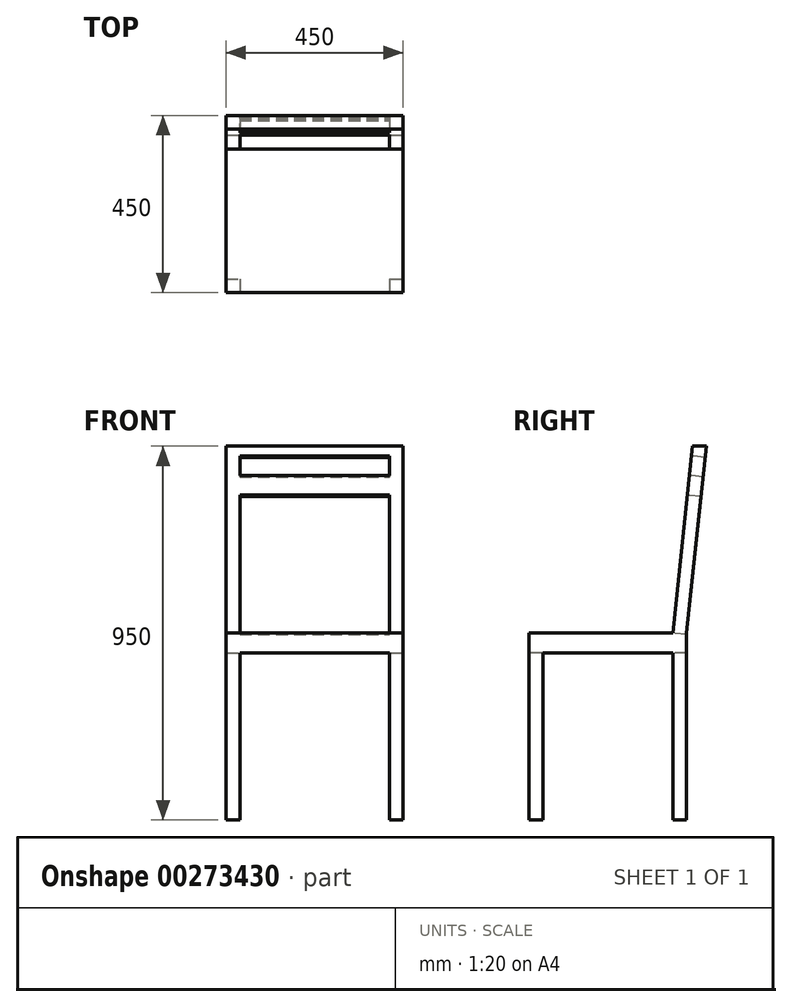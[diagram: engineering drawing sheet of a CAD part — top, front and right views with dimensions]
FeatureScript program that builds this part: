
annotation { "Feature Type Name" : "Feature", "Feature Type Description" : "" }
export const myFeature = defineFeature(function(context is Context, id is Id, definition is map)
    precondition{}
    {
        {
            var Q0;
            Q0=qCreatedBy(makeId("Top.planeOp"),FACE);
            var sketch = newSketch(context, id + "F0", { "sketchPlane" : qUnion([Q0])});
            skLineSegment(sketch, "E0.bottom", {"start": v(225, 225) * mm, "end": v(-225, 225) * mm});
            skLineSegment(sketch, "E0.top", {"start": v(225, -225) * mm, "end": v(-225, -225) * mm});
            skLineSegment(sketch, "E0.left", {"start": v(225, 225) * mm, "end": v(225, -225) * mm});
            skLineSegment(sketch, "E0.right", {"start": v(-225, 225) * mm, "end": v(-225, -225) * mm});
            skPoint(sketch, "E0.middle", {"position": v(0, 0) * mm});
            skSolve(sketch);
        }
        {
            var Q0;
            Q0=qSketchRegion(id+"F0",true);
            extrude(context, id + "F1", {"entities" : qUnion([Q0]), "depth" : 950 * mm});
        }
        {
            var Q0;
            Q0=makeQuery(id+"F1.opExtrude","SWEPT_FACE",FACE,{"disambiguationData":[OSD([sQuery(id+"F0.wireOp",EDGE,"E0.left")])]});
            var sketch = newSketch(context, id + "F2", { "sketchPlane" : qUnion([Q0])});
            skLineSegment(sketch, "E1.bottom", {"start": v(225, 475) * mm, "end": v(-225, 475) * mm});
            skLineSegment(sketch, "E1.top", {"start": v(225, 425) * mm, "end": v(-225, 425) * mm});
            skLineSegment(sketch, "E1.left", {"start": v(225, 475) * mm, "end": v(225, 425) * mm});
            skLineSegment(sketch, "E1.right", {"start": v(-225, 475) * mm, "end": v(-225, 425) * mm});
            skLineSegment(sketch, "E2", {"start": v(225, 950) * mm, "end": v(175, 475) * mm});
            skLineSegment(sketch, "E3", {"start": v(190, 950) * mm, "end": v(140, 475) * mm});
            skLineSegment(sketch, "E4", {"start": v(175, 475) * mm, "end": v(175, 0) * mm});
            skLineSegment(sketch, "E5", {"start": v(140, 0) * mm, "end": v(140, 475) * mm});
            skLineSegment(sketch, "E6.bottom", {"start": v(-225, 0) * mm, "end": v(-190, 0) * mm});
            skLineSegment(sketch, "E6.top", {"start": v(-225, 425) * mm, "end": v(-190, 425) * mm});
            skLineSegment(sketch, "E6.left", {"start": v(-225, 0) * mm, "end": v(-225, 425) * mm});
            skLineSegment(sketch, "E6.right", {"start": v(-190, 0) * mm, "end": v(-190, 425) * mm});
            skSolve(sketch);
        }
        {
            var Q0;
            {var subQ4=sQuery(id+"F2.wireOp",EDGE,"E3");Q0=makeQuery(id+"F2.imprint","IMPRINT",FACE,{"disambiguationData":[TD([[makeQuery(id+"F2.imprint","IMPRINT",EDGE,{"derivedFrom":subQ4}),-1.0]])]});}
            var Q1;
            {var subQ4=sQuery(id+"F2.wireOp",EDGE,"E2");Q1=makeQuery(id+"F2.imprint","IMPRINT",FACE,{"disambiguationData":[TD([[makeQuery(id+"F2.imprint","IMPRINT",EDGE,{"derivedFrom":subQ4}),1.0]])]});}
            var Q2;
            {var subQ0=sQuery(id+"F2.wireOp",EDGE,"E1.left");Q2=makeQuery(id+"F2.imprint","IMPRINT",FACE,{"disambiguationData":[TD([[makeQuery(id+"F2.imprint","IMPRINT",EDGE,{"derivedFrom":subQ0}),-1.0]])]});}
            var Q3;
            {var subQ1=sQuery(id+"F0.wireOp",EDGE,"E0.left");var subQ4=sQuery(id+"F2.wireOp",EDGE,"E4");var subQ6=makeQuery(id+"F1.opExtrude","CAP_EDGE",EDGE,{"disambiguationData":[OSD([subQ1])],"isStart":true});var subQ7=makeQuery(id+"F2.imprint","INTERSECT",VERTEX,{"derivedFrom":[subQ6,subQ4]});Q3=makeQuery(id+"F2.imprint","IMPRINT",FACE,{"disambiguationData":[TD([[makeQuery(id+"F2.imprint","IMPRINT",EDGE,{"disambiguationData":[TD([[subQ7,1.0]])],"derivedFrom":subQ4}),1.0]])]});}
            var Q4;
            {var subQ0=sQuery(id+"F2.wireOp",EDGE,"E6.right");Q4=makeQuery(id+"F2.imprint","IMPRINT",FACE,{"disambiguationData":[TD([[makeQuery(id+"F2.imprint","IMPRINT",EDGE,{"derivedFrom":subQ0}),-1.0]])]});}
            extrude(context, id + "F3", {"entities" : qUnion([Q0, Q1, Q2, Q3, Q4]), "operationType" : NewBodyOperationType.REMOVE, "endBound" : BoundingType.THROUGH_ALL, "oppositeDirection" : true, "depth" : 25 * mm});
        }
        {
            var Q0;
            Q0=makeQuery(id+"F1.opExtrude","SWEPT_FACE",FACE,{"disambiguationData":[OSD([sQuery(id+"F0.wireOp",EDGE,"E0.top")])]});
            var sketch = newSketch(context, id + "F4", { "sketchPlane" : qUnion([Q0])});
            skLineSegment(sketch, "E7", {"start": v(-190, 0) * mm, "end": v(-190, 425) * mm});
            skLineSegment(sketch, "E8", {"start": v(-190, 425) * mm, "end": v(190, 425) * mm});
            skLineSegment(sketch, "E9", {"start": v(190, 425) * mm, "end": v(190, 0) * mm});
            skSolve(sketch);
        }
        {
            var Q0;
            Q0 = qSketchRegion(id + "F4", true);
            var Q1;
            {var subQ0=sQuery(id+"F4.wireOp",EDGE,"E7");Q1=makeQuery(id+"F4.imprint","IMPRINT",FACE,{"disambiguationData":[TD([[makeQuery(id+"F4.imprint","IMPRINT",EDGE,{"derivedFrom":subQ0}),-1.0]])]});}
            extrude(context, id + "F5", {"entities" : qUnion([Q0, Q1]), "operationType" : NewBodyOperationType.REMOVE, "endBound" : BoundingType.THROUGH_ALL, "oppositeDirection" : true, "depth" : 25 * mm});
        }
        {
            var Q0;
            Q0=makeQuery(id+"F3.boolean.opBoolean","COPY",FACE,{"derivedFrom":makeQuery(id+"F3.opExtrude","SWEPT_FACE",FACE,{"disambiguationData":[OSD([sQuery(id+"F2.wireOp",EDGE,"E3")])]})});
            var sketch = newSketch(context, id + "F6", { "sketchPlane" : qUnion([Q0])});
            skLineSegment(sketch, "E10", {"start": v(-190, 487.05) * mm, "end": v(-190, 939.67) * mm});
            skLineSegment(sketch, "E11", {"start": v(-190, 939.67) * mm, "end": v(190, 939.67) * mm});
            skLineSegment(sketch, "E12", {"start": v(190, 939.67) * mm, "end": v(190, 487.05) * mm});
            skLineSegment(sketch, "E13", {"start": v(-190, 889.67) * mm, "end": v(190, 889.67) * mm});
            skLineSegment(sketch, "E14", {"start": v(-190, 839.67) * mm, "end": v(190, 839.67) * mm});
            skSolve(sketch);
        }
        {
            var Q0;
            {var subQ0=sQuery(id+"F6.wireOp",EDGE,"E11");Q0=makeQuery(id+"F6.imprint","IMPRINT",FACE,{"disambiguationData":[TD([[makeQuery(id+"F6.imprint","IMPRINT",EDGE,{"derivedFrom":subQ0}),-1.0]])]});}
            var Q1;
            {var subQ3=sQuery(id+"F6.wireOp",EDGE,"E14");Q1=makeQuery(id+"F6.imprint","IMPRINT",FACE,{"disambiguationData":[TD([[makeQuery(id+"F6.imprint","IMPRINT",EDGE,{"derivedFrom":subQ3}),-1.0]])]});}
            extrude(context, id + "F7", {"entities" : qUnion([Q0, Q1]), "operationType" : NewBodyOperationType.REMOVE, "endBound" : BoundingType.THROUGH_ALL, "oppositeDirection" : true, "depth" : 25 * mm});
        }
    });
